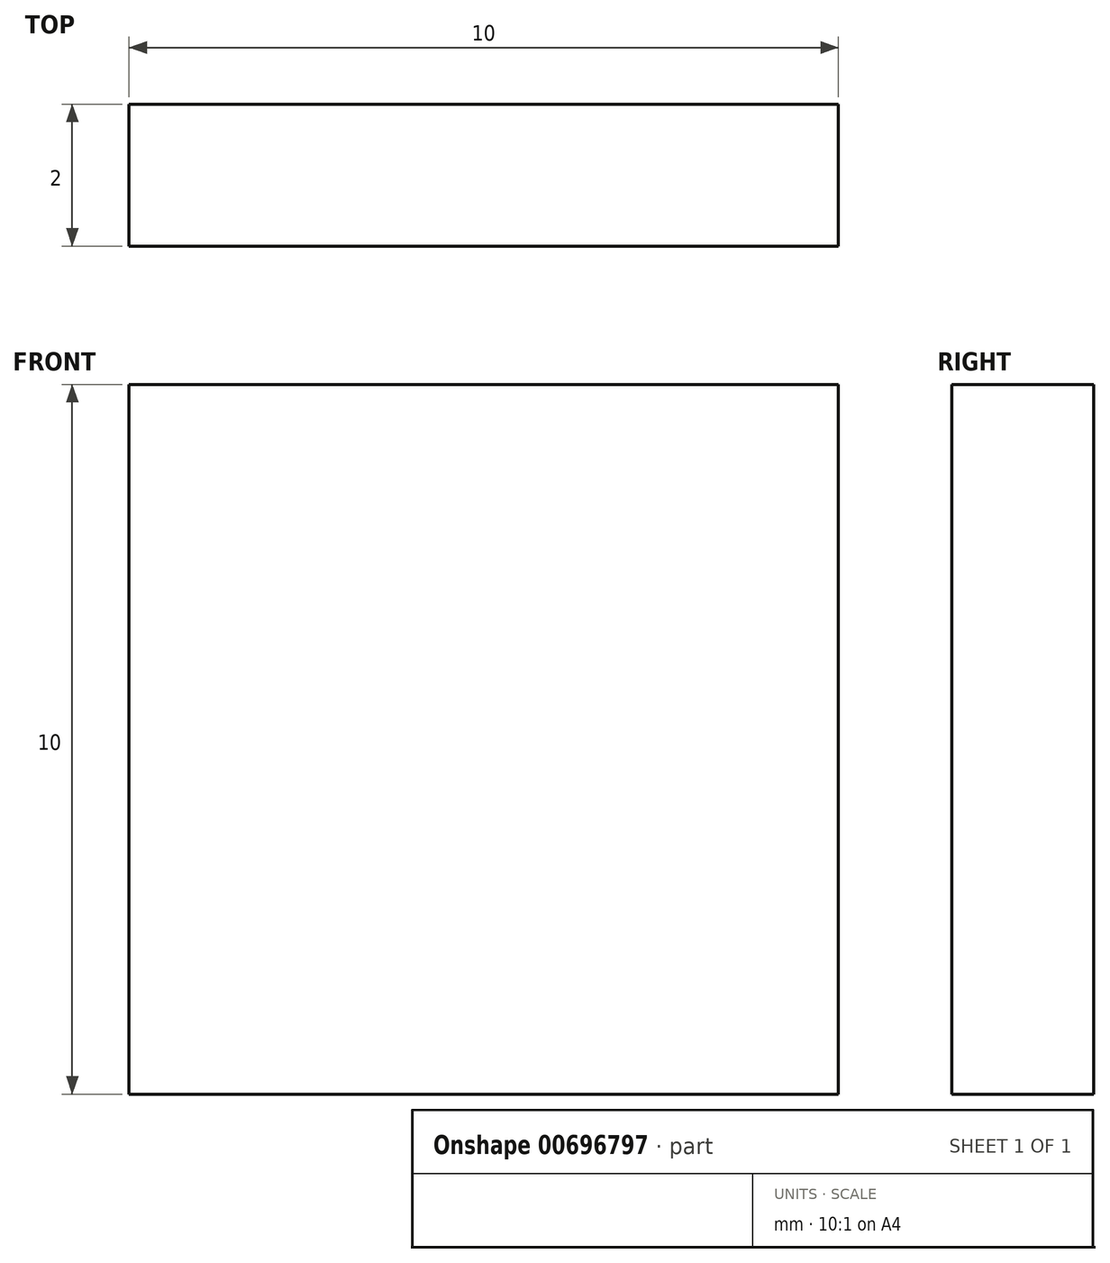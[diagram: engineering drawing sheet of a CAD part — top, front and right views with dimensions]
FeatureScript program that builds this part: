
annotation { "Feature Type Name" : "Feature", "Feature Type Description" : "" }
export const myFeature = defineFeature(function(context is Context, id is Id, definition is map)
    precondition{}
    {
        {
            var Q0;
            Q0=qCreatedBy(makeId("Front.planeOp"),FACE);
            var sketch = newSketch(context, id + "F0", { "sketchPlane" : qUnion([Q0])});
            skLineSegment(sketch, "E0.bottom", {"start": v(5, -5) * mm, "end": v(-5, -5) * mm});
            skLineSegment(sketch, "E0.top", {"start": v(5, 5) * mm, "end": v(-5, 5) * mm});
            skLineSegment(sketch, "E0.left", {"start": v(5, -5) * mm, "end": v(5, 5) * mm});
            skLineSegment(sketch, "E0.right", {"start": v(-5, -5) * mm, "end": v(-5, 5) * mm});
            skPoint(sketch, "E0.middle", {"position": v(0, 0) * mm});
            skSolve(sketch);
        }
        {
            var Q0;
            Q0=makeQuery(id+"F0.imprint","IMPRINT",FACE,{"disambiguationData":[TD([[makeQuery(id+"F0.imprint","IMPRINT",EDGE,{"derivedFrom":sQuery(id+"F0.wireOp",EDGE,"E0.bottom")}),-1.0]])]});
            extrude(context, id + "F1", {"entities" : qUnion([Q0]), "depth" : 2 * mm, "offsetDistance" : 25 * mm});
        }
    });
